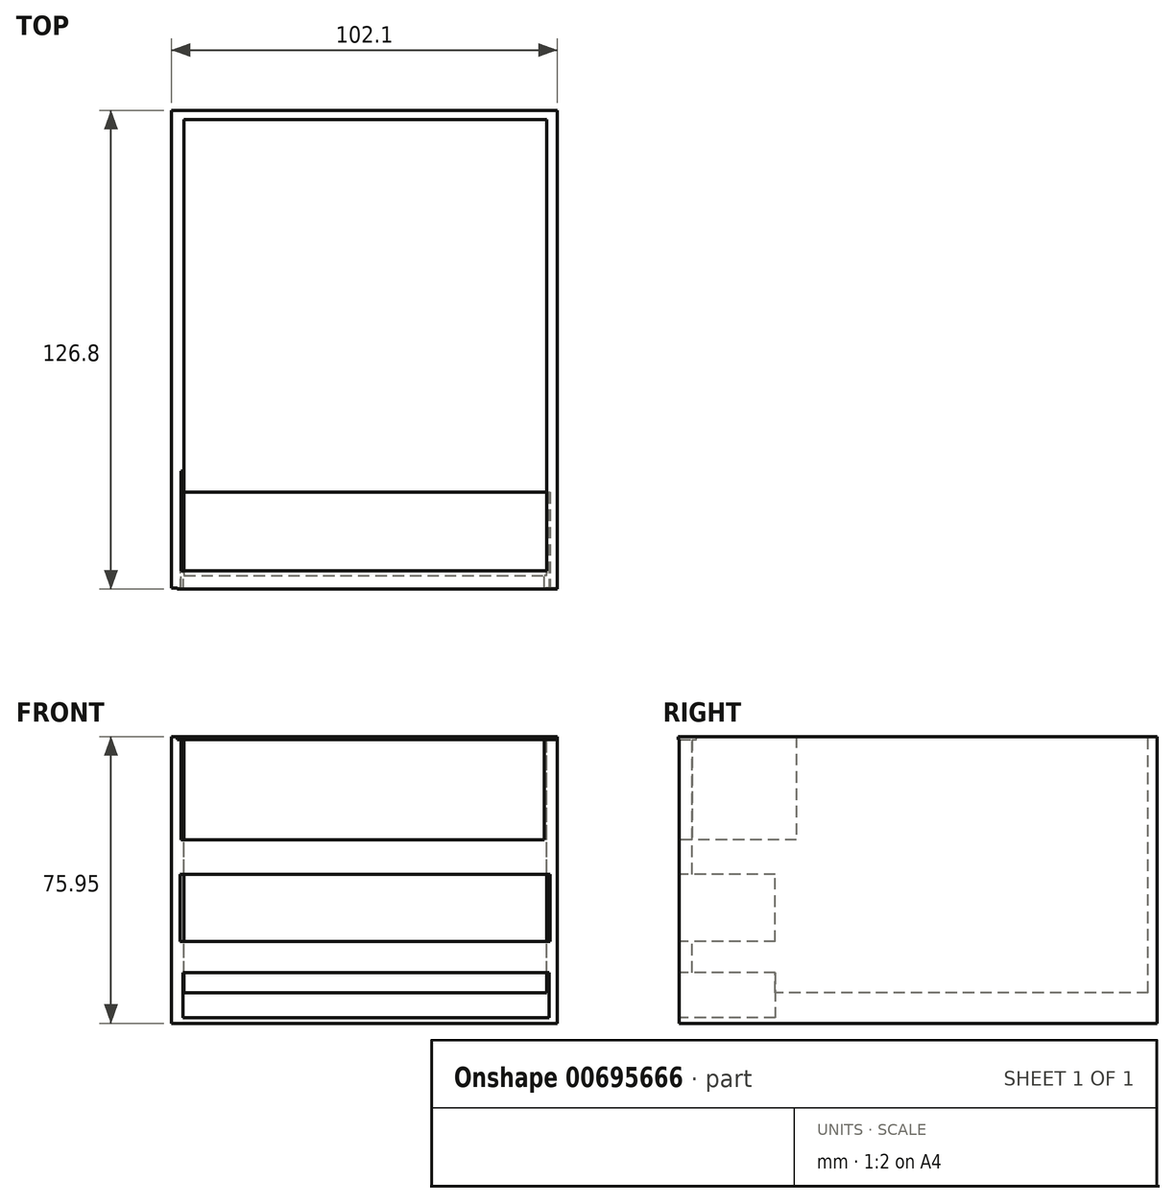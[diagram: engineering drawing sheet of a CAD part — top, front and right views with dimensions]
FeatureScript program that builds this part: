
annotation { "Feature Type Name" : "Feature", "Feature Type Description" : "" }
export const myFeature = defineFeature(function(context is Context, id is Id, definition is map)
    precondition{}
    {
        {
            var Q0;
            Q0=qCreatedBy(makeId("Top.planeOp"),FACE);
            var sketch = newSketch(context, id + "F0", { "sketchPlane" : qUnion([Q0])});
            skLineSegment(sketch, "E0.bottom", {"start": v(-50.44, 59.74) * mm, "end": v(51.66, 59.74) * mm});
            skLineSegment(sketch, "E0.top", {"start": v(-50.44, -66.75) * mm, "end": v(51.66, -66.75) * mm});
            skLineSegment(sketch, "E0.left", {"start": v(-50.44, 59.74) * mm, "end": v(-50.44, -66.75) * mm});
            skLineSegment(sketch, "E0.right", {"start": v(51.66, 59.74) * mm, "end": v(51.66, -66.75) * mm});
            skSolve(sketch);
        }
        {
            var Q0;
            Q0=makeQuery(id+"F0.imprint","IMPRINT",FACE,{"disambiguationData":[TD([[makeQuery(id+"F0.imprint","IMPRINT",EDGE,{"derivedFrom":sQuery(id+"F0.wireOp",EDGE,"E0.bottom")}),-1.0]])]});
            extrude(context, id + "F1", {"entities" : qUnion([Q0]), "oppositeDirection" : true, "depth" : 75.95 * mm, "offsetDistance" : 25.4 * mm});
        }
        {
            var Q0;
            Q0=makeQuery(id+"F1.opExtrude","CAP_FACE",FACE,{"disambiguationData":[OSD([sQuery(id+"F0.wireOp",EDGE,"E0.bottom"),sQuery(id+"F0.wireOp",EDGE,"E0.top"),sQuery(id+"F0.wireOp",EDGE,"E0.left"),sQuery(id+"F0.wireOp",EDGE,"E0.right")])],"isStart":true});
            var sketch = newSketch(context, id + "F2", { "sketchPlane" : qUnion([Q0])});
            skLineSegment(sketch, "E1.bottom", {"start": v(-47.1, 57.3) * mm, "end": v(48.92, 57.3) * mm});
            skLineSegment(sketch, "E1.top", {"start": v(-47.1, -63.4) * mm, "end": v(48.92, -63.4) * mm});
            skLineSegment(sketch, "E1.left", {"start": v(-47.1, 57.3) * mm, "end": v(-47.1, -63.4) * mm});
            skLineSegment(sketch, "E1.right", {"start": v(48.92, 57.3) * mm, "end": v(48.92, -63.4) * mm});
            skSolve(sketch);
        }
        {
            var Q0;
            Q0=makeQuery(id+"F2.imprint","IMPRINT",FACE,{"disambiguationData":[TD([[makeQuery(id+"F2.imprint","IMPRINT",EDGE,{"derivedFrom":sQuery(id+"F2.wireOp",EDGE,"E1.bottom")}),-1.0]])]});
            extrude(context, id + "F3", {"entities" : qUnion([Q0]), "operationType" : NewBodyOperationType.REMOVE, "oppositeDirection" : true, "depth" : 67.82 * mm, "offsetDistance" : 25.4 * mm});
        }
        {
            var Q0;
            Q0=makeQuery(id+"F1.opExtrude","SWEPT_FACE",FACE,{"disambiguationData":[OSD([sQuery(id+"F0.wireOp",EDGE,"E0.top")])]});
            var sketch = newSketch(context, id + "F4", { "sketchPlane" : qUnion([Q0])});
            skLineSegment(sketch, "E2", {"start": v(-50.44, -34.45) * mm, "end": v(51.66, -34.45) * mm});
            skLineSegment(sketch, "E3", {"start": v(51.66, -34.45) * mm, "end": v(51.66, -27.64) * mm});
            skLineSegment(sketch, "E4", {"start": v(51.66, -27.64) * mm, "end": v(-50.44, -27.64) * mm});
            skLineSegment(sketch, "E5", {"start": v(-50.44, -27.64) * mm, "end": v(-50.44, -56.22) * mm});
            skLineSegment(sketch, "E6", {"start": v(-50.44, -56.22) * mm, "end": v(51.66, -56.22) * mm});
            skLineSegment(sketch, "E7", {"start": v(51.66, -56.22) * mm, "end": v(51.66, -61.54) * mm});
            skLineSegment(sketch, "E8", {"start": v(51.66, -61.54) * mm, "end": v(-50.44, -61.54) * mm});
            skLineSegment(sketch, "E9", {"start": v(-50.44, -61.54) * mm, "end": v(-50.44, -56.22) * mm});
            skSolve(sketch);
        }
        {
            var Q0;
            {var subQ0=sQuery(id+"F4.wireOp",EDGE,"E4");Q0=makeQuery(id+"F4.imprint","IMPRINT",FACE,{"disambiguationData":[TD([[makeQuery(id+"F4.imprint","IMPRINT",EDGE,{"derivedFrom":subQ0}),-1.0]])]});}
            var sketch = newSketch(context, id + "F5", { "sketchPlane" : qUnion([Q0])});
            skLineSegment(sketch, "E10.bottom", {"start": v(-47.94, 0) * mm, "end": v(48.28, 0) * mm});
            skLineSegment(sketch, "E10.top", {"start": v(-47.94, -27.31) * mm, "end": v(48.28, -27.31) * mm});
            skLineSegment(sketch, "E10.left", {"start": v(-47.94, 0) * mm, "end": v(-47.94, -27.31) * mm});
            skLineSegment(sketch, "E10.right", {"start": v(48.28, 0) * mm, "end": v(48.28, -27.31) * mm});
            skSolve(sketch);
        }
        {
            var Q0;
            Q0=makeQuery(id+"F5.imprint","IMPRINT",FACE,{"disambiguationData":[TD([[makeQuery(id+"F5.imprint","IMPRINT",EDGE,{"derivedFrom":sQuery(id+"F5.wireOp",EDGE,"E10.bottom")}),-1.0]])]});
            extrude(context, id + "F6", {"entities" : qUnion([Q0]), "operationType" : NewBodyOperationType.REMOVE, "oppositeDirection" : true, "depth" : 30.99 * mm, "offsetDistance" : 25.4 * mm});
        }
        {
            var Q0;
            {var subQ0=sQuery(id+"F4.wireOp",EDGE,"E2");Q0=makeQuery(id+"F4.imprint","IMPRINT",FACE,{"disambiguationData":[TD([[makeQuery(id+"F4.imprint","IMPRINT",EDGE,{"derivedFrom":subQ0}),-1.0]])]});}
            var sketch = newSketch(context, id + "F7", { "sketchPlane" : qUnion([Q0])});
            skLineSegment(sketch, "E11.bottom", {"start": v(-48.14, -36.5) * mm, "end": v(49.77, -36.5) * mm});
            skLineSegment(sketch, "E11.top", {"start": v(-48.14, -54.3) * mm, "end": v(49.77, -54.3) * mm});
            skLineSegment(sketch, "E11.left", {"start": v(-48.14, -36.5) * mm, "end": v(-48.14, -54.3) * mm});
            skLineSegment(sketch, "E11.right", {"start": v(49.77, -36.5) * mm, "end": v(49.77, -54.3) * mm});
            skSolve(sketch);
        }
        {
            var Q0;
            Q0=makeQuery(id+"F7.imprint","IMPRINT",FACE,{"disambiguationData":[TD([[makeQuery(id+"F7.imprint","IMPRINT",EDGE,{"derivedFrom":sQuery(id+"F7.wireOp",EDGE,"E11.bottom")}),-1.0]])]});
            extrude(context, id + "F8", {"entities" : qUnion([Q0]), "operationType" : NewBodyOperationType.REMOVE, "oppositeDirection" : true, "depth" : 25.4 * mm, "offsetDistance" : 25.4 * mm});
        }
        {
            var Q0;
            {var subQ0=sQuery(id+"F4.wireOp",EDGE,"E8");Q0=makeQuery(id+"F4.imprint","IMPRINT",FACE,{"disambiguationData":[TD([[makeQuery(id+"F4.imprint","IMPRINT",EDGE,{"derivedFrom":subQ0}),1.0]])]});}
            var sketch = newSketch(context, id + "F9", { "sketchPlane" : qUnion([Q0])});
            skLineSegment(sketch, "E12.bottom", {"start": v(-47.35, -62.54) * mm, "end": v(49.51, -62.54) * mm});
            skLineSegment(sketch, "E12.top", {"start": v(-47.35, -74.53) * mm, "end": v(49.51, -74.53) * mm});
            skLineSegment(sketch, "E12.left", {"start": v(-47.35, -62.54) * mm, "end": v(-47.35, -74.53) * mm});
            skLineSegment(sketch, "E12.right", {"start": v(49.51, -62.54) * mm, "end": v(49.51, -74.53) * mm});
            skSolve(sketch);
        }
        {
            var Q0;
            Q0=makeQuery(id+"F9.imprint","IMPRINT",FACE,{"disambiguationData":[TD([[makeQuery(id+"F9.imprint","IMPRINT",EDGE,{"derivedFrom":sQuery(id+"F9.wireOp",EDGE,"E12.bottom")}),-1.0]])]});
            extrude(context, id + "F10", {"entities" : qUnion([Q0]), "operationType" : NewBodyOperationType.REMOVE, "oppositeDirection" : true, "depth" : 25.4 * mm, "offsetDistance" : 25.4 * mm});
        }
        {
            var Q0;
            Q0=qCreatedBy(makeId("Top.planeOp"),FACE);
            var sketch = newSketch(context, id + "F11", { "sketchPlane" : qUnion([Q0])});
            skLineSegment(sketch, "E13.bottom", {"start": v(-48.92, -62.18) * mm, "end": v(51.66, -62.18) * mm});
            skLineSegment(sketch, "E13.top", {"start": v(-48.92, -67.06) * mm, "end": v(51.66, -67.06) * mm});
            skLineSegment(sketch, "E13.left", {"start": v(-48.92, -62.18) * mm, "end": v(-48.92, -67.06) * mm});
            skLineSegment(sketch, "E13.right", {"start": v(51.66, -62.18) * mm, "end": v(51.66, -67.06) * mm});
            skSolve(sketch);
        }
        {
            var Q0;
            Q0=makeQuery(id+"F11.imprint","IMPRINT",FACE,{"disambiguationData":[TD([[makeQuery(id+"F11.imprint","IMPRINT",EDGE,{"derivedFrom":sQuery(id+"F11.wireOp",EDGE,"E13.bottom")}),-1.0]])]});
            extrude(context, id + "F12", {"entities" : qUnion([Q0]), "operationType" : NewBodyOperationType.ADD, "oppositeDirection" : true, "depth" : 0.76 * mm, "offsetDistance" : 25.4 * mm});
        }
    });
